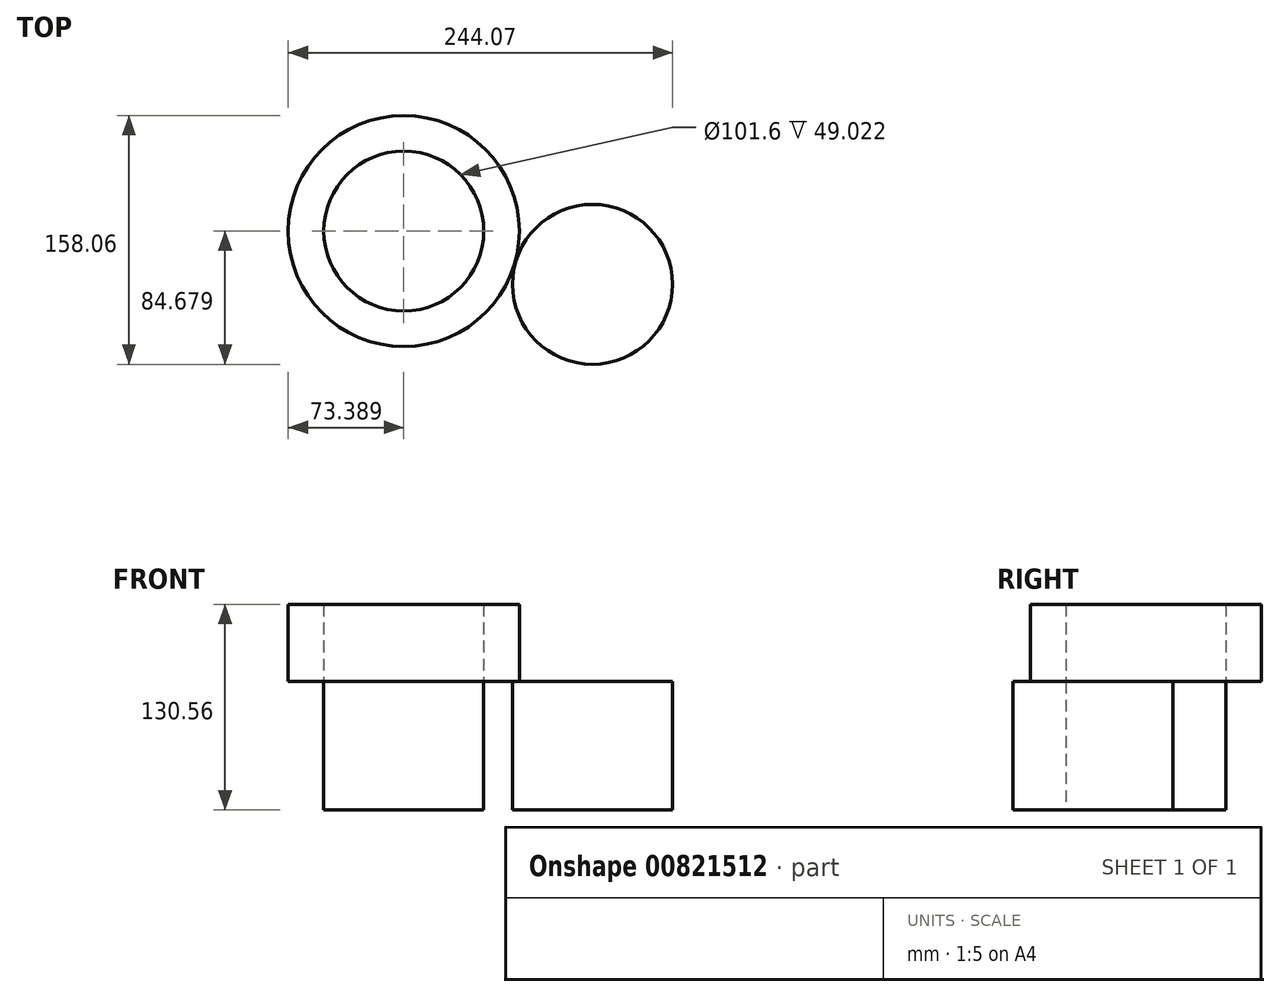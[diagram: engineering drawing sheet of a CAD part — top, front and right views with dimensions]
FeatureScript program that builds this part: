
annotation { "Feature Type Name" : "Feature", "Feature Type Description" : "" }
export const myFeature = defineFeature(function(context is Context, id is Id, definition is map)
    precondition{}
    {
        {
            var Q0;
            Q0=qCreatedBy(makeId("Top.planeOp"),FACE);
            var sketch = newSketch(context, id + "F0", { "sketchPlane" : qUnion([Q0])});
            skCircle(sketch, "E0", {"center": v(0, 0) * mm, "radius": 50.8 * mm});
            skCircle(sketch, "E1", {"center": v(-119.88, 33.88) * mm, "radius": 50.8 * mm});
            skSolve(sketch);
        }
        {
            var Q0;
            Q0=makeQuery(id+"F0.imprint","IMPRINT",FACE,{"disambiguationData":[TD([[makeQuery(id+"F0.imprint","IMPRINT",EDGE,{"derivedFrom":sQuery(id+"F0.wireOp",EDGE,"E1")}),1.0]])]});
            var Q1;
            Q1=makeQuery(id+"F0.imprint","IMPRINT",FACE,{"disambiguationData":[TD([[makeQuery(id+"F0.imprint","IMPRINT",EDGE,{"derivedFrom":sQuery(id+"F0.wireOp",EDGE,"E0")}),1.0]])]});
            extrude(context, id + "F1", {"entities" : qUnion([Q0, Q1]), "depth" : 81.53 * mm, "offsetDistance" : 25.4 * mm});
        }
        {
            var Q0;
            Q0=makeQuery(id+"F1.opExtrude","CAP_FACE",FACE,{"disambiguationData":[OSD([sQuery(id+"F0.wireOp",EDGE,"E1")])],"isStart":false});
            var sketch = newSketch(context, id + "F2", { "sketchPlane" : qUnion([Q0])});
            skCircle(sketch, "E2", {"center": v(-119.88, 33.88) * mm, "radius": 73.39 * mm});
            skSolve(sketch);
        }
        {
            var Q0;
            Q0=makeQuery(id+"F2.imprint","IMPRINT",FACE,{"disambiguationData":[TD([[makeQuery(id+"F2.imprint","IMPRINT",EDGE,{"derivedFrom":sQuery(id+"F2.wireOp",EDGE,"E2")}),1.0]])]});
            extrude(context, id + "F3", {"entities" : qUnion([Q0]), "depth" : 49.02 * mm, "offsetDistance" : 25.4 * mm});
        }
    });
